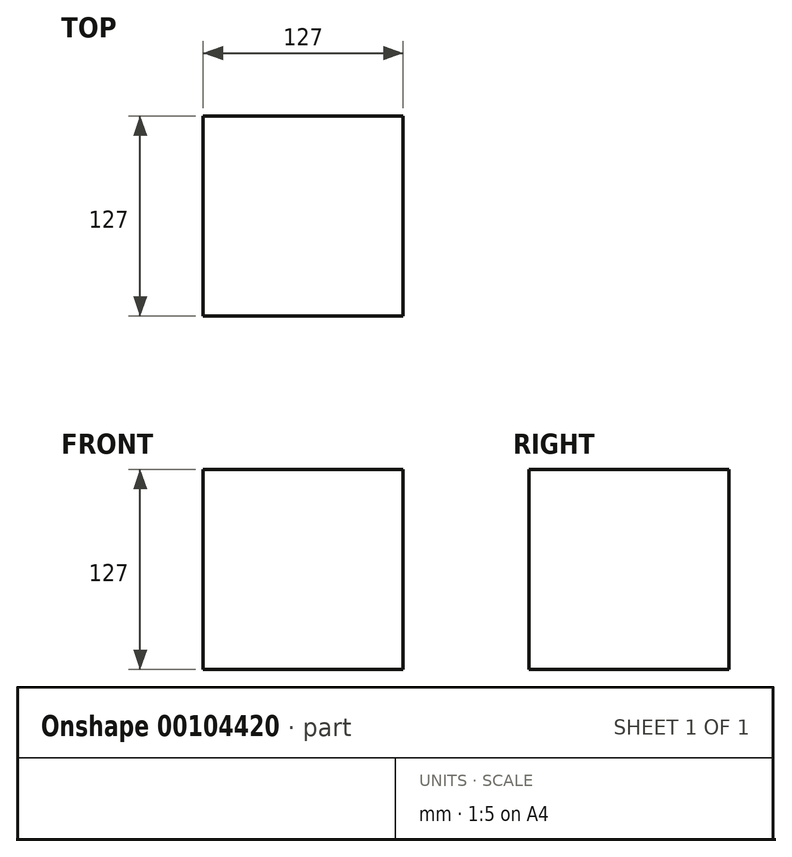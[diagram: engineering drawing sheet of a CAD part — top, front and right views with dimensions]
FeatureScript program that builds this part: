
annotation { "Feature Type Name" : "Feature", "Feature Type Description" : "" }
export const myFeature = defineFeature(function(context is Context, id is Id, definition is map)
    precondition{}
    {
        {
            var Q0;
            Q0=qCreatedBy(makeId("Front.planeOp"),FACE);
            var sketch = newSketch(context, id + "F0", { "sketchPlane" : qUnion([Q0])});
            skLineSegment(sketch, "E0.bottom", {"start": v(-63.5, 63.5) * mm, "end": v(63.5, 63.5) * mm});
            skLineSegment(sketch, "E0.top", {"start": v(-63.5, -63.5) * mm, "end": v(63.5, -63.5) * mm});
            skLineSegment(sketch, "E0.left", {"start": v(-63.5, 63.5) * mm, "end": v(-63.5, -63.5) * mm});
            skLineSegment(sketch, "E0.right", {"start": v(63.5, 63.5) * mm, "end": v(63.5, -63.5) * mm});
            skSolve(sketch);
        }
        {
            var Q0;
            Q0 = qSketchRegion(id + "F0", true);
            extrude(context, id + "F1", {"entities" : qUnion([Q0]), "depth" : 63.5 * mm, "hasSecondDirection" : true, "secondDirectionOppositeDirection" : true, "secondDirectionDepth" : 63.5 * mm});
        }
    });
